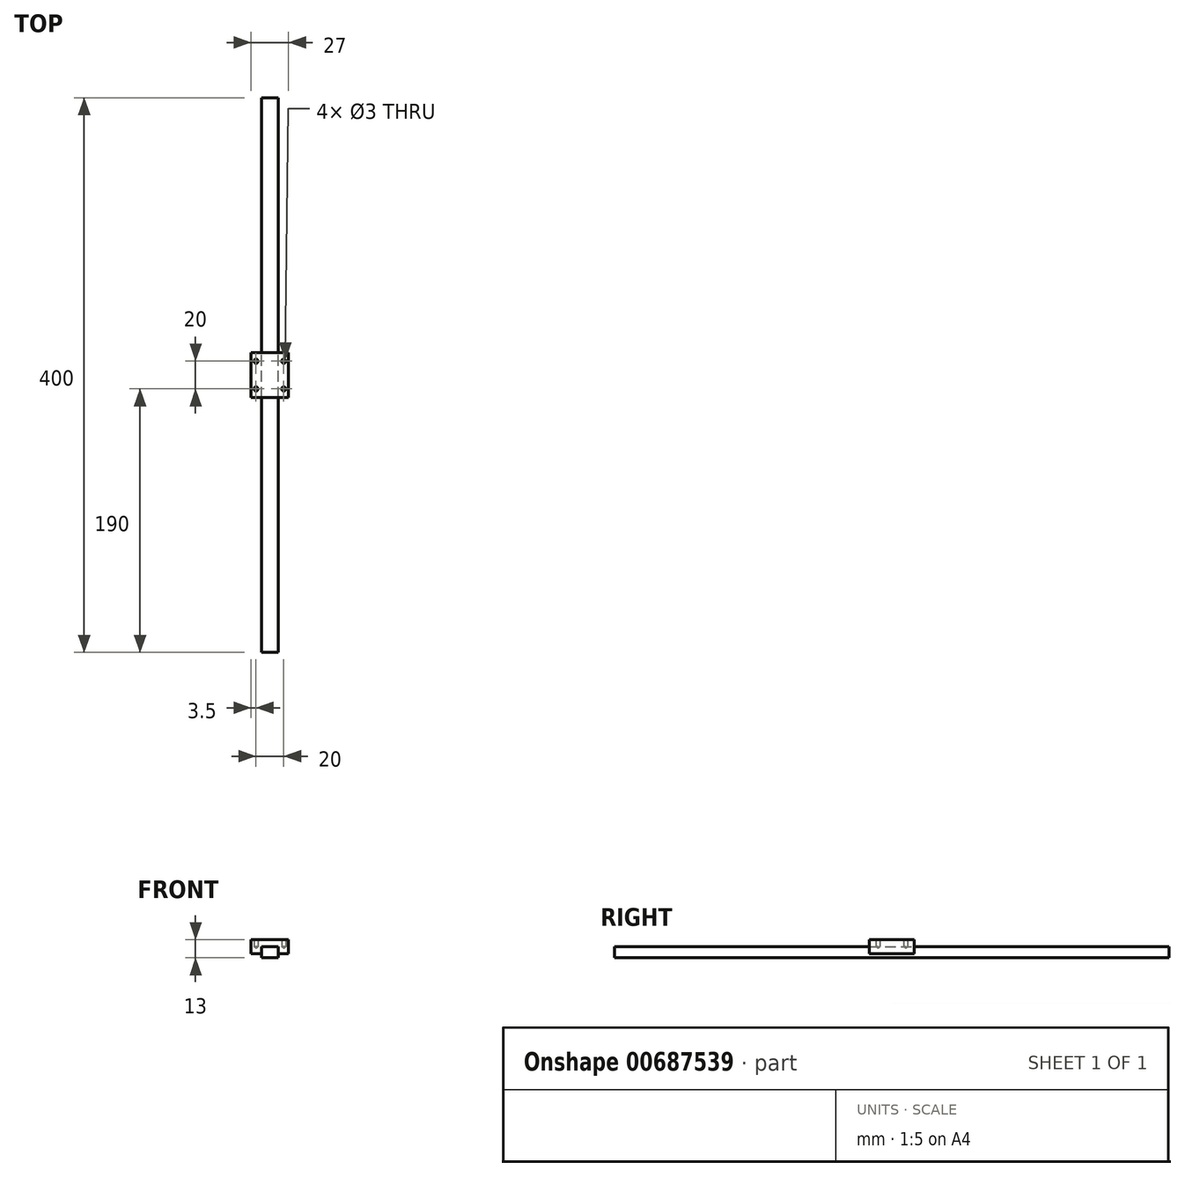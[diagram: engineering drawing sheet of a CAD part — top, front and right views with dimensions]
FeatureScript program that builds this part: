
annotation { "Feature Type Name" : "Feature", "Feature Type Description" : "" }
export const myFeature = defineFeature(function(context is Context, id is Id, definition is map)
    precondition{}
    {
        {
            var Q0;
            Q0=qCreatedBy(makeId("Front.planeOp"),FACE);
            var sketch = newSketch(context, id + "F0", { "sketchPlane" : qUnion([Q0])});
            skLineSegment(sketch, "E0.bottom", {"start": v(-6, 0) * mm, "end": v(6, 0) * mm});
            skLineSegment(sketch, "E0.top", {"start": v(-6, 8) * mm, "end": v(6, 8) * mm});
            skLineSegment(sketch, "E0.left", {"start": v(-6, 0) * mm, "end": v(-6, 8) * mm});
            skLineSegment(sketch, "E0.right", {"start": v(6, 0) * mm, "end": v(6, 8) * mm});
            skLineSegment(sketch, "E1", {"start": v(0, 8) * mm, "end": v(0, 0) * mm, "construction": true});
            skLineSegment(sketch, "E2", {"start": v(-6, 3) * mm, "end": v(-13.5, 3) * mm});
            skLineSegment(sketch, "E3", {"start": v(-13.5, 3) * mm, "end": v(-13.5, 13) * mm});
            skLineSegment(sketch, "E4", {"start": v(-13.5, 13) * mm, "end": v(13.5, 13) * mm});
            skLineSegment(sketch, "E5", {"start": v(13.5, 13) * mm, "end": v(13.5, 3) * mm});
            skLineSegment(sketch, "E6", {"start": v(13.5, 3) * mm, "end": v(6, 3) * mm});
            skSolve(sketch);
        }
        {
            var Q0;
            {var subQ3=sQuery(id+"F0.wireOp",EDGE,"E0.bottom");Q0=makeQuery(id+"F0.imprint","IMPRINT",FACE,{"disambiguationData":[TD([[makeQuery(id+"F0.imprint","IMPRINT",EDGE,{"derivedFrom":subQ3}),1.0]])]});}
            extrude(context, id + "F1", {"entities" : qUnion([Q0]), "depth" : 400 * mm, "offsetDistance" : 25 * mm, "symmetric" : true});
        }
        {
            var Q0;
            {var subQ1=sQuery(id+"F0.wireOp",EDGE,"E0.top");Q0=makeQuery(id+"F0.imprint","IMPRINT",FACE,{"disambiguationData":[TD([[makeQuery(id+"F0.imprint","IMPRINT",EDGE,{"derivedFrom":subQ1}),1.0]])]});}
            extrude(context, id + "F2", {"entities" : qUnion([Q0]), "depth" : 32.4 * mm, "offsetDistance" : 25 * mm, "symmetric" : true});
        }
        {
            var Q0;
            Q0=makeQuery(id+"F2.opExtrude","SWEPT_FACE",FACE,{"disambiguationData":[OSD([sQuery(id+"F0.wireOp",EDGE,"E4")])]});
            var sketch = newSketch(context, id + "F3", { "sketchPlane" : qUnion([Q0])});
            skLineSegment(sketch, "E7.bottom", {"start": v(10, 10) * mm, "end": v(-10, 10) * mm, "construction": true});
            skLineSegment(sketch, "E7.top", {"start": v(10, -10) * mm, "end": v(-10, -10) * mm, "construction": true});
            skLineSegment(sketch, "E7.left", {"start": v(10, 10) * mm, "end": v(10, -10) * mm, "construction": true});
            skLineSegment(sketch, "E7.right", {"start": v(-10, 10) * mm, "end": v(-10, -10) * mm, "construction": true});
            skPoint(sketch, "E7.middle", {"position": v(0, 0) * mm});
            skCircle(sketch, "E8", {"center": v(-10, 10) * mm, "radius": 1.5 * mm});
            skCircle(sketch, "E9", {"center": v(10, 10) * mm, "radius": 1.5 * mm});
            skCircle(sketch, "E10", {"center": v(10, -10) * mm, "radius": 1.5 * mm});
            skCircle(sketch, "E11", {"center": v(-10, -10) * mm, "radius": 1.5 * mm});
            skSolve(sketch);
        }
        {
            var Q0;
            Q0=sQuery(id+"F3.wireOp",VERTEX,"E8.center");
            var Q1;
            Q1=sQuery(id+"F3.wireOp",VERTEX,"E9.center");
            var Q2;
            Q2=sQuery(id+"F3.wireOp",VERTEX,"E10.center");
            var Q3;
            Q3=sQuery(id+"F3.wireOp",VERTEX,"E11.center");
            var Q4;
            Q4=makeQuery(id+"F2.opExtrude","SWEPT_BODY",BODY,{"disambiguationData":[OSD([sQuery(id+"F0.wireOp",EDGE,"E0.top"),sQuery(id+"F0.wireOp",EDGE,"E0.left"),sQuery(id+"F0.wireOp",EDGE,"E0.right"),sQuery(id+"F0.wireOp",EDGE,"E2"),sQuery(id+"F0.wireOp",EDGE,"E3"),sQuery(id+"F0.wireOp",EDGE,"E4"),sQuery(id+"F0.wireOp",EDGE,"E5"),sQuery(id+"F0.wireOp",EDGE,"E6")])]});
            hole(context, id + "F4", {"style" : HoleStyle.SIMPLE, "endStyle" : HoleEndStyle.BLIND, "holeDiameter" : 3 * mm, "majorDiameter" : 5 * mm, "holeDepth" : 5 * mm, "isTappedThrough" : true, "tappedDepth" : 12 * mm, "tapClearance" : 3, "startFromSketch" : true, "locations" : qUnion([Q0, Q1, Q2, Q3]), "scope" : qUnion([Q4])});
        }
    });
